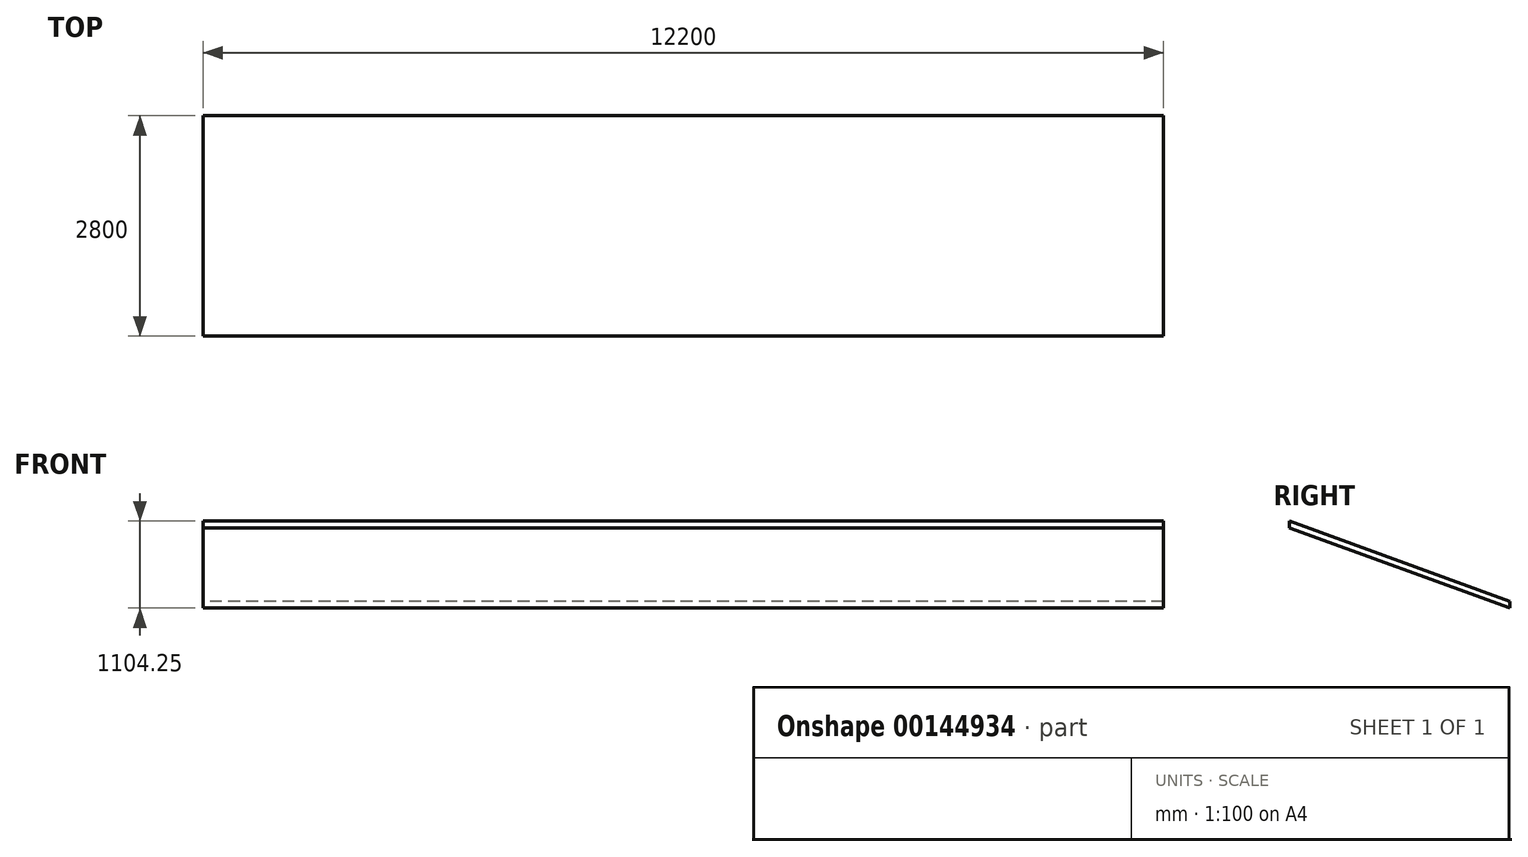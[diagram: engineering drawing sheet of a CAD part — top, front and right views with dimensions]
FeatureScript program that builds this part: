
annotation { "Feature Type Name" : "Feature", "Feature Type Description" : "" }
export const myFeature = defineFeature(function(context is Context, id is Id, definition is map)
    precondition{}
    {
        {
            var Q0;
            Q0=qCreatedBy(makeId("Right.planeOp"),FACE);
            var sketch = newSketch(context, id + "F0", { "sketchPlane" : qUnion([Q0])});
            skLineSegment(sketch, "E0", {"start": v(0, 0) * mm, "end": v(2800, -1019.12) * mm});
            skLineSegment(sketch, "E1", {"start": v(0, 0) * mm, "end": v(-170.8, 0) * mm, "construction": true});
            skLineSegment(sketch, "E2.0", {"start": v(0, 85.13) * mm, "end": v(2800, -933.98) * mm});
            skLineSegment(sketch, "E3", {"start": v(0, 85.13) * mm, "end": v(0, 0) * mm});
            skLineSegment(sketch, "E4", {"start": v(2800, -933.98) * mm, "end": v(2800, -1019.12) * mm});
            skSolve(sketch);
        }
        {
            var Q0;
            Q0 = qSketchRegion(id + "F0", true);
            extrude(context, id + "F1", {"entities" : qUnion([Q0]), "depth" : 12200 * mm});
        }
    });
